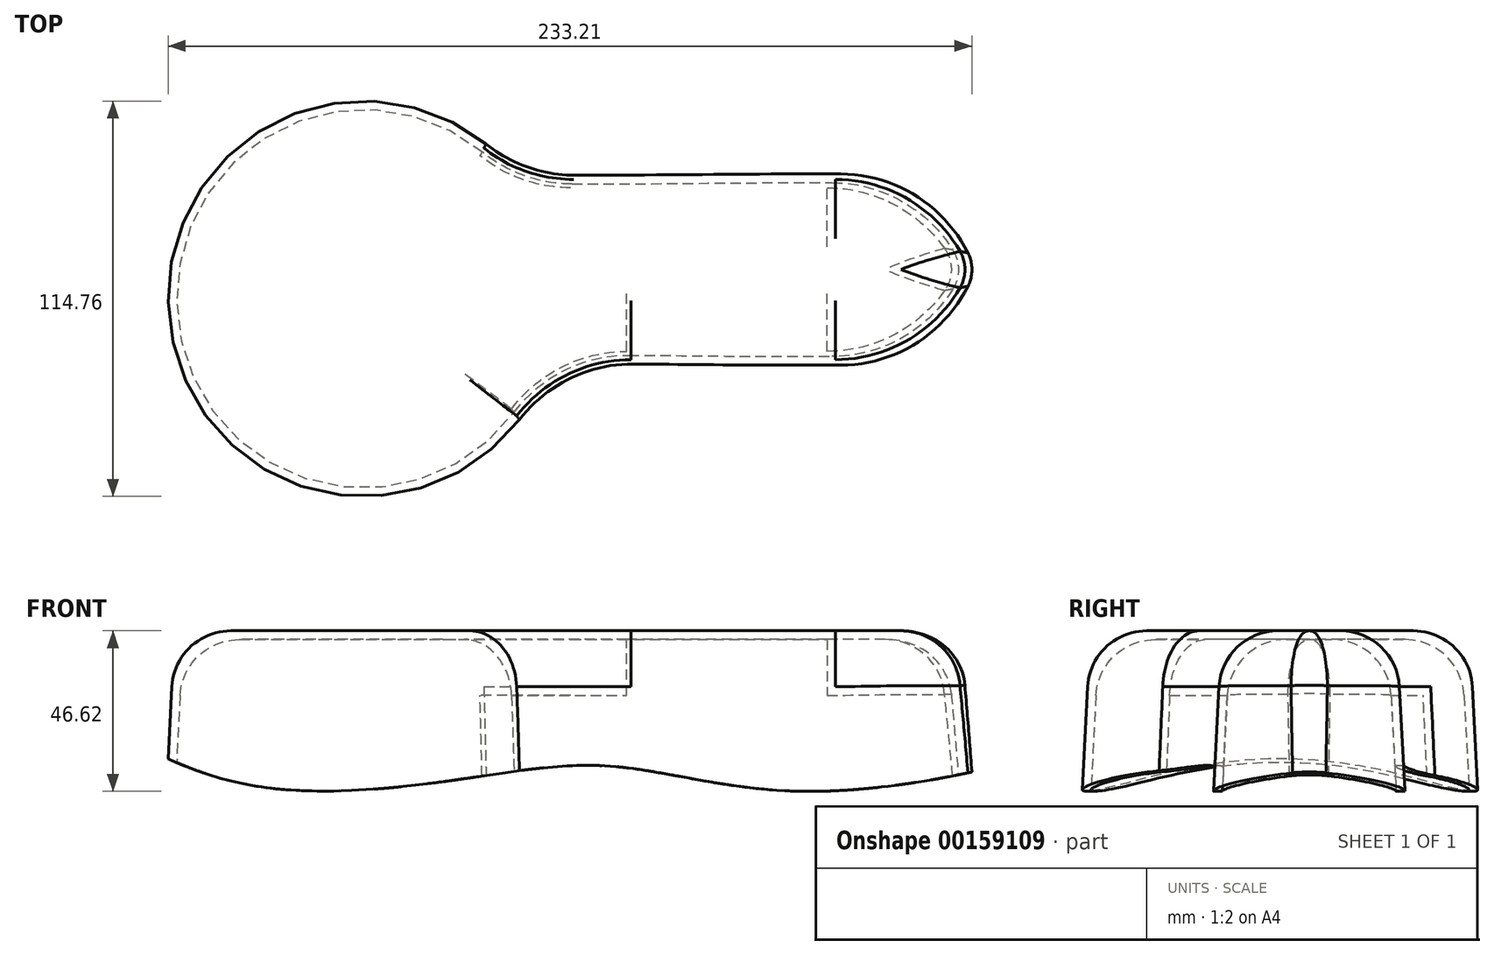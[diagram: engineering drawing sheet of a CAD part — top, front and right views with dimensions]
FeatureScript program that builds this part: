
annotation { "Feature Type Name" : "Feature", "Feature Type Description" : "" }
export const myFeature = defineFeature(function(context is Context, id is Id, definition is map)
    precondition{}
    {
        {
            var Q0;
            Q0=qCreatedBy(makeId("Top.planeOp"),FACE);
            var sketch = newSketch(context, id + "F0", { "sketchPlane" : qUnion([Q0])});
            skArc(sketch, "E0", {"start": v(-9.56, 26.13) * mm, "mid": v(-112.96, -21.45) * mm, "end": v(0.32, -32.5) * mm});
            skLineSegment(sketch, "E1.bottom", {"start": v(-9.56, 26.13) * mm, "end": v(126.78, 26.13) * mm});
            skLineSegment(sketch, "E1.top", {"start": v(0.32, -32.5) * mm, "end": v(126.78, -32.5) * mm});
            skLineSegment(sketch, "E1.right", {"start": v(126.78, 26.13) * mm, "end": v(126.78, -32.5) * mm});
            skSolve(sketch);
        }
        {
            var Q0;
            Q0 = qSketchRegion(id + "F0", true);
            extrude(context, id + "F1", {"entities" : qUnion([Q0]), "depth" : 76.2 * mm, "hasDraft" : true, "draftAngle" : 3 * degree, "draftPullDirection" : true});
        }
        {
            var Q0;
            Q0=makeQuery(id+"F1.opExtrude","CAP_FACE",FACE,{"disambiguationData":[OSD([sQuery(id+"F0.wireOp",EDGE,"E0"),sQuery(id+"F0.wireOp",EDGE,"E1.bottom"),sQuery(id+"F0.wireOp",EDGE,"E1.top"),sQuery(id+"F0.wireOp",EDGE,"E1.right")])],"isStart":true});
            shell(context, id + "F2", {"entities" : qUnion([Q0]), "thickness" : 2.54 * mm});
        }
        {
            var Q0;
            Q0=makeQuery(id+"F1.opExtrude","SWEPT_EDGE",EDGE,{"disambiguationData":[OSD([sQuery(id+"F0.wireOp",EDGE,"E0"),sQuery(id+"F0.wireOp",EDGE,"E1.bottom")])]});
            var Q1;
            Q1=makeQuery(id+"F1.opExtrude","SWEPT_EDGE",EDGE,{"disambiguationData":[OSD([sQuery(id+"F0.wireOp",EDGE,"E0"),sQuery(id+"F0.wireOp",EDGE,"E1.top")])]});
            var Q2;
            Q2=makeQuery(id+"F2.opShell","OFFSET_EDGE",EDGE,{"disambiguationData":[OSD([sQuery(id+"F0.wireOp",EDGE,"E0"),sQuery(id+"F0.wireOp",EDGE,"E1.bottom")])]});
            var Q3;
            Q3=makeQuery(id+"F2.opShell","OFFSET_EDGE",EDGE,{"disambiguationData":[OSD([sQuery(id+"F0.wireOp",EDGE,"E0"),sQuery(id+"F0.wireOp",EDGE,"E1.top")])]});
            var Q4;
            Q4=makeQuery(id+"F2.opShell","OFFSET_EDGE",EDGE,{"disambiguationData":[OSD([sQuery(id+"F0.wireOp",EDGE,"E1.bottom"),sQuery(id+"F0.wireOp",EDGE,"E1.right")])]});
            var Q5;
            Q5=makeQuery(id+"F2.opShell","OFFSET_EDGE",EDGE,{"disambiguationData":[OSD([sQuery(id+"F0.wireOp",EDGE,"E1.top"),sQuery(id+"F0.wireOp",EDGE,"E1.right")])]});
            var Q6;
            Q6=makeQuery(id+"F1.opExtrude","SWEPT_EDGE",EDGE,{"disambiguationData":[OSD([sQuery(id+"F0.wireOp",EDGE,"E1.bottom"),sQuery(id+"F0.wireOp",EDGE,"E1.right")])]});
            var Q7;
            Q7=makeQuery(id+"F1.opExtrude","SWEPT_EDGE",EDGE,{"disambiguationData":[OSD([sQuery(id+"F0.wireOp",EDGE,"E1.top"),sQuery(id+"F0.wireOp",EDGE,"E1.right")])]});
            fillet(context, id + "F3", {"entities" : qUnion([Q0, Q1, Q2, Q3, Q4, Q5, Q6, Q7]), "radius" : 41.83 * mm, "tangentPropagation" : true, "allowEdgeOverflow" : false});
        }
        {
            var Q0;
            Q0=makeQuery(id+"F2.opShell","OFFSET_FACE",FACE,{"disambiguationData":[OSD([sQuery(id+"F0.wireOp",EDGE,"E0"),sQuery(id+"F0.wireOp",EDGE,"E1.bottom"),sQuery(id+"F0.wireOp",EDGE,"E1.top"),sQuery(id+"F0.wireOp",EDGE,"E1.right")])]});
            var Q1;
            Q1=makeQuery(id+"F1.opExtrude","CAP_FACE",FACE,{"disambiguationData":[OSD([sQuery(id+"F0.wireOp",EDGE,"E0"),sQuery(id+"F0.wireOp",EDGE,"E1.bottom"),sQuery(id+"F0.wireOp",EDGE,"E1.top"),sQuery(id+"F0.wireOp",EDGE,"E1.right")])],"isStart":false});
            fillet(context, id + "F4", {"entities" : qUnion([Q0, Q1]), "radius" : 17.17 * mm, "tangentPropagation" : true, "allowEdgeOverflow" : false});
        }
        {
            var Q0;
            {var subQ0=sQuery(id+"F0.wireOp",EDGE,"E1.right");Q0=makeQuery(id+"F3.opFillet","BLEND_EDGE",EDGE,{"blendedFrom":[makeQuery(id+"F2.opShell","OFFSET_EDGE",EDGE,{"disambiguationData":[OSD([sQuery(id+"F0.wireOp",EDGE,"E1.bottom"),subQ0])]}),makeQuery(id+"F2.opShell","OFFSET_EDGE",EDGE,{"disambiguationData":[OSD([sQuery(id+"F0.wireOp",EDGE,"E1.top"),subQ0])]})],"blendedInto":[]});}
            var Q1;
            {var subQ0=sQuery(id+"F0.wireOp",EDGE,"E1.right");Q1=makeQuery(id+"F3.opFillet","BLEND_EDGE",EDGE,{"blendedFrom":[makeQuery(id+"F1.opExtrude","SWEPT_EDGE",EDGE,{"disambiguationData":[OSD([sQuery(id+"F0.wireOp",EDGE,"E1.bottom"),subQ0])]}),makeQuery(id+"F1.opExtrude","SWEPT_EDGE",EDGE,{"disambiguationData":[OSD([sQuery(id+"F0.wireOp",EDGE,"E1.top"),subQ0])]})],"blendedInto":[]});}
            fillet(context, id + "F5", {"entities" : qUnion([Q0, Q1]), "radius" : 10.6 * mm, "tangentPropagation" : true, "allowEdgeOverflow" : false});
        }
        {
            var Q0;
            Q0=makeQuery(id+"F1.opExtrude","SWEPT_FACE",FACE,{"disambiguationData":[OSD([sQuery(id+"F0.wireOp",EDGE,"E1.top")])]});
            var Q1;
            Q1=makeQuery(id+"F1.opExtrude","SWEPT_FACE",FACE,{"disambiguationData":[OSD([sQuery(id+"F0.wireOp",EDGE,"E1.bottom")])]});
            cPlane(context, id + "F6", {"entities" : qUnion([Q0, Q1]), "cplaneType" : CPlaneType.MID_PLANE, "offset" : 25.4 * mm, "width" : 152.4 * mm, "height" : 152.4 * mm});
        }
        {
            var Q0;
            Q0=qCreatedBy(id+"F6.planeOp",FACE);
            var sketch = newSketch(context, id + "F7", { "sketchPlane" : qUnion([Q0])});
            skFitSpline(sketch, "E2", {"points": [v(-135.7, 51.77) * mm, v(-88.1, 31.42) * mm, v(-25.97, 33.23) * mm, v(16.9, 36.87) * mm, v(72.13, 29.6) * mm, v(150.26, 43.4) * mm, v(173.15, 55.4) * mm], "startDerivative": vector(266.55, -153.16) * mm, "endDerivative": vector(154.7, 101.3) * mm});
            skLineSegment(sketch, "E3", {"start": v(-135.7, 51.77) * mm, "end": v(-135.7, -34.71) * mm});
            skLineSegment(sketch, "E4", {"start": v(-135.7, -34.71) * mm, "end": v(173.15, -34.71) * mm});
            skLineSegment(sketch, "E5", {"start": v(173.15, -34.71) * mm, "end": v(173.15, 55.4) * mm});
            skSolve(sketch);
        }
        {
            var Q0;
            Q0 = qSketchRegion(id + "F7", true);
            extrude(context, id + "F8", {"entities" : qUnion([Q0]), "operationType" : NewBodyOperationType.REMOVE, "depth" : 185.42 * mm, "symmetric" : true});
        }
    });
